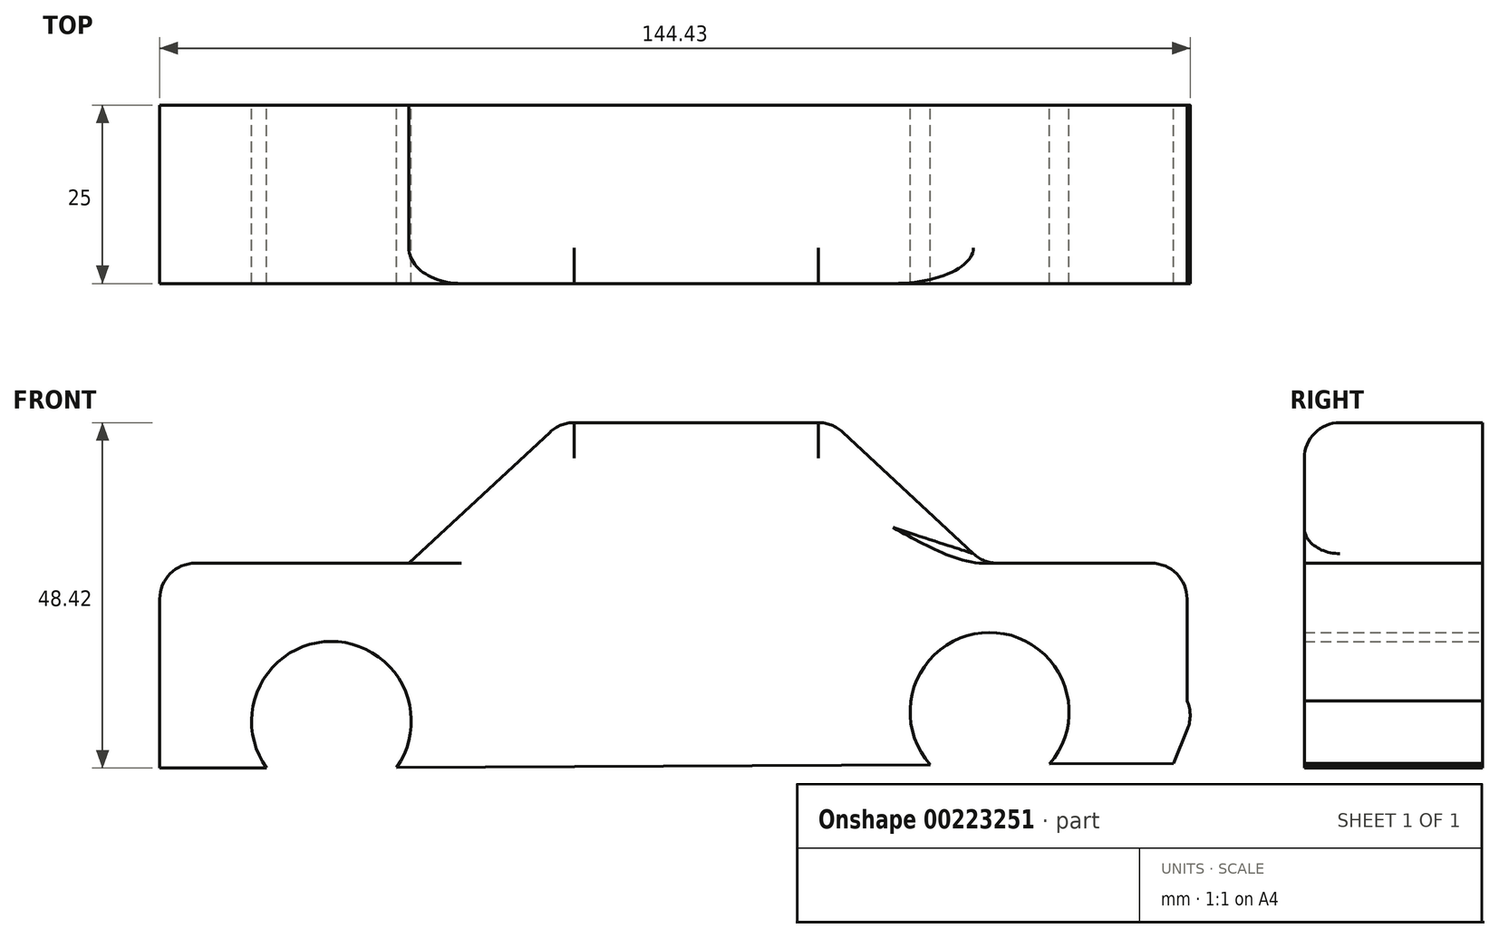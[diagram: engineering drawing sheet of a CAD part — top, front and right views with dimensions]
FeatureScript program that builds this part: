
annotation { "Feature Type Name" : "Feature", "Feature Type Description" : "" }
export const myFeature = defineFeature(function(context is Context, id is Id, definition is map)
    precondition{}
    {
        {
            var Q0;
            Q0=qCreatedBy(makeId("Front.planeOp"),FACE);
            var sketch = newSketch(context, id + "F0", { "sketchPlane" : qUnion([Q0])});
            skLineSegment(sketch, "E0", {"start": v(-71.9, 0) * mm, "end": v(-36.96, 0) * mm});
            skLineSegment(sketch, "E1", {"start": v(-36.96, 0) * mm, "end": v(-15.75, 19.71) * mm});
            skLineSegment(sketch, "E2", {"start": v(-15.75, 19.71) * mm, "end": v(22.4, 19.71) * mm});
            skLineSegment(sketch, "E3", {"start": v(22.4, 19.71) * mm, "end": v(43.6, 0) * mm});
            skLineSegment(sketch, "E4", {"start": v(43.6, 0) * mm, "end": v(72.1, 0) * mm});
            skLineSegment(sketch, "E5", {"start": v(72.1, 0) * mm, "end": v(72.1, -19.28) * mm});
            skLineSegment(sketch, "E6", {"start": v(72.1, -19.28) * mm, "end": v(73.76, -19.28) * mm});
            skLineSegment(sketch, "E7", {"start": v(73.76, -19.28) * mm, "end": v(70.2, -28.07) * mm});
            skLineSegment(sketch, "E8", {"start": v(-71.9, 0) * mm, "end": v(-71.9, -28.71) * mm});
            skLineSegment(sketch, "E9", {"start": v(-71.9, -28.71) * mm, "end": v(-56.9, -28.71) * mm});
            skLineSegment(sketch, "E10", {"start": v(-38.68, -28.62) * mm, "end": v(36.1, -28.24) * mm});
            skArc(sketch, "E11", {"start": v(-38.68, -28.62) * mm, "mid": v(-47.88, -10.96) * mm, "end": v(-56.9, -28.71) * mm});
            skArc(sketch, "E12", {"start": v(52.82, -28.16) * mm, "mid": v(44.37, -9.7) * mm, "end": v(36.1, -28.24) * mm});
            skLineSegment(sketch, "E13.trimOffspring", {"start": v(52.82, -28.16) * mm, "end": v(70.2, -28.07) * mm});
            skSolve(sketch);
        }
        {
            var Q0;
            Q0=makeQuery(id+"F0.imprint","IMPRINT",FACE,{"disambiguationData":[TD([[makeQuery(id+"F0.imprint","IMPRINT",EDGE,{"derivedFrom":sQuery(id+"F0.wireOp",EDGE,"E0")}),-1.0]])]});
            extrude(context, id + "F1", {"entities" : qUnion([Q0]), "depth" : 25 * mm});
        }
        {
            var Q0;
            Q0=makeQuery(id+"F1.opExtrude","CAP_EDGE",EDGE,{"disambiguationData":[OSD([sQuery(id+"F0.wireOp",EDGE,"E2")])],"isStart":false});
            var Q1;
            Q1=makeQuery(id+"F1.opExtrude","SWEPT_EDGE",EDGE,{"disambiguationData":[OSD([sQuery(id+"F0.wireOp",EDGE,"E6"),sQuery(id+"F0.wireOp",EDGE,"E7")])]});
            var Q2;
            Q2=makeQuery(id+"F1.opExtrude","SWEPT_EDGE",EDGE,{"disambiguationData":[OSD([sQuery(id+"F0.wireOp",EDGE,"E0"),sQuery(id+"F0.wireOp",EDGE,"E8")])]});
            var Q3;
            Q3=makeQuery(id+"F1.opExtrude","SWEPT_EDGE",EDGE,{"disambiguationData":[OSD([sQuery(id+"F0.wireOp",EDGE,"E4"),sQuery(id+"F0.wireOp",EDGE,"E5")])]});
            fillet(context, id + "F2", {"entities" : qUnion([Q0, Q1, Q2, Q3]), "radius" : 5 * mm, "tangentPropagation" : true, "allowEdgeOverflow" : false});
        }
        {
            var Q0;
            Q0=makeQuery(id+"F1.opExtrude","CAP_EDGE",EDGE,{"disambiguationData":[OSD([sQuery(id+"F0.wireOp",EDGE,"E3")])],"isStart":false});
            fillet(context, id + "F3", {"entities" : qUnion([Q0]), "radius" : 5 * mm, "tangentPropagation" : true, "allowEdgeOverflow" : false});
        }
        {
            var Q0;
            Q0=makeQuery(id+"F3.opFillet","BLEND_FACE",FACE,{"disambiguationData":[OSD([sQuery(id+"F0.wireOp",EDGE,"E3")])]});
            fillet(context, id + "F4", {"entities" : qUnion([Q0]), "radius" : 5 * mm, "tangentPropagation" : true, "allowEdgeOverflow" : false});
        }
        {
            var Q0;
            Q0=makeQuery(id+"F1.opExtrude","CAP_EDGE",EDGE,{"disambiguationData":[OSD([sQuery(id+"F0.wireOp",EDGE,"E1")])],"isStart":false});
            fillet(context, id + "F5", {"entities" : qUnion([Q0]), "radius" : 5 * mm, "tangentPropagation" : true, "allowEdgeOverflow" : false});
        }
    });
